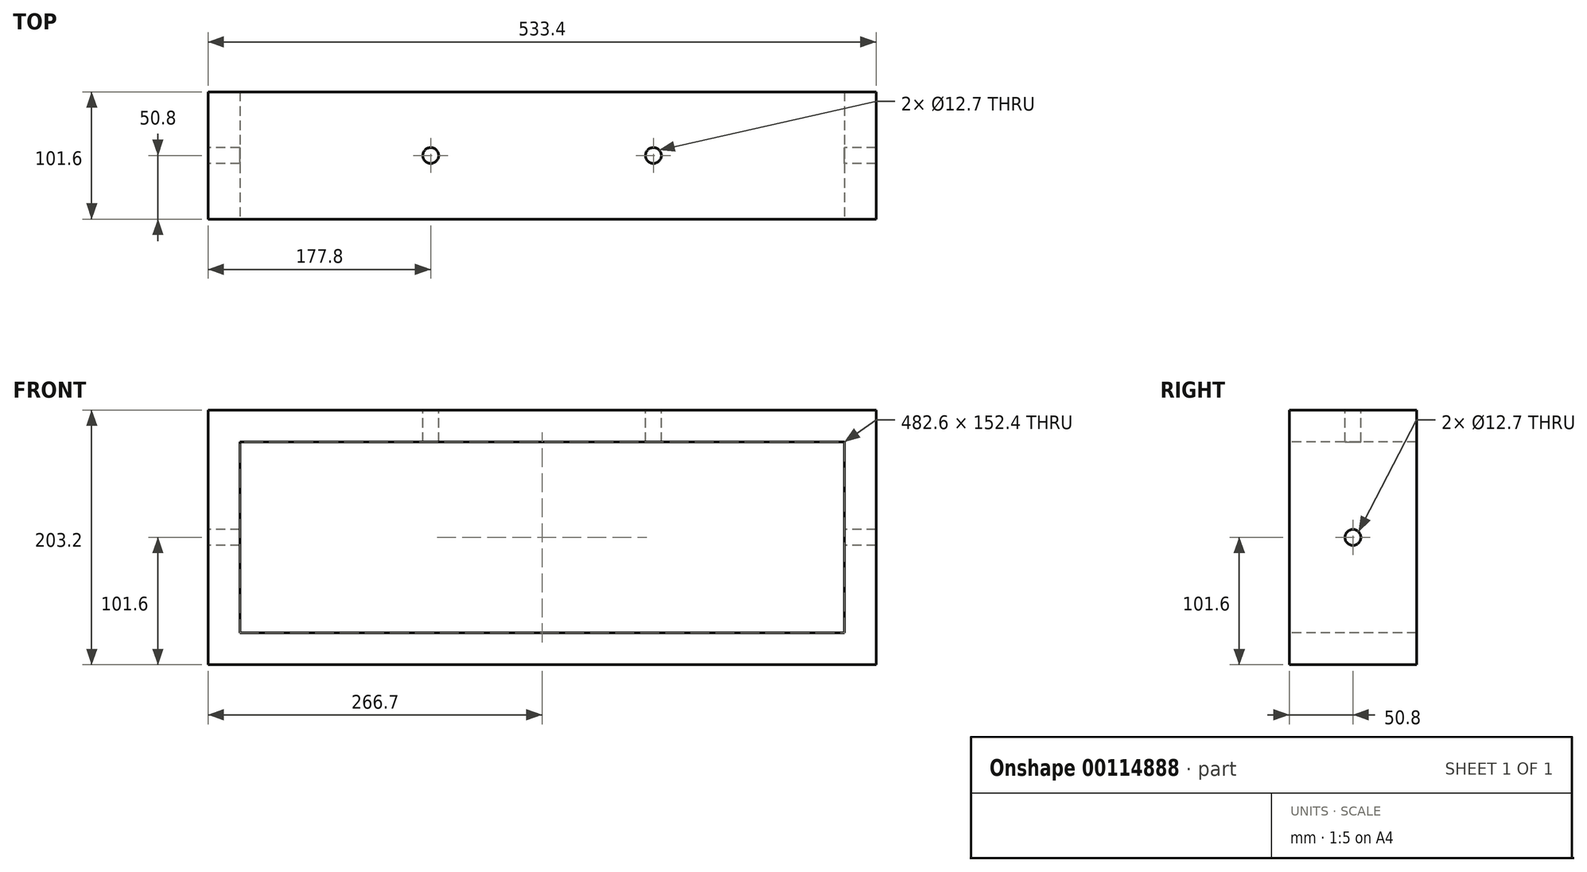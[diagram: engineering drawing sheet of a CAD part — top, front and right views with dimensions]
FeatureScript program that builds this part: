
annotation { "Feature Type Name" : "Feature", "Feature Type Description" : "" }
export const myFeature = defineFeature(function(context is Context, id is Id, definition is map)
    precondition{}
    {
        {
            var Q0;
            Q0=qCreatedBy(makeId("Front.planeOp"),FACE);
            var sketch = newSketch(context, id + "F0", { "sketchPlane" : qUnion([Q0])});
            skLineSegment(sketch, "E0.bottom", {"start": v(-266.7, 101.6) * mm, "end": v(266.7, 101.6) * mm});
            skLineSegment(sketch, "E0.top", {"start": v(-266.7, -101.6) * mm, "end": v(266.7, -101.6) * mm});
            skLineSegment(sketch, "E0.left", {"start": v(-266.7, 101.6) * mm, "end": v(-266.7, -101.6) * mm});
            skLineSegment(sketch, "E0.right", {"start": v(266.7, 101.6) * mm, "end": v(266.7, -101.6) * mm});
            skPoint(sketch, "E0.middle", {"position": v(0, 0) * mm});
            skLineSegment(sketch, "E1", {"start": v(-266.7, 101.6) * mm, "end": v(-266.7, 76.2) * mm});
            skLineSegment(sketch, "E2", {"start": v(-266.7, 76.2) * mm, "end": v(266.7, 76.2) * mm});
            skLineSegment(sketch, "E3", {"start": v(-266.7, 76.2) * mm, "end": v(-241.3, 76.2) * mm});
            skLineSegment(sketch, "E4", {"start": v(-241.3, 76.2) * mm, "end": v(-241.3, -101.6) * mm});
            skLineSegment(sketch, "E5", {"start": v(266.7, 76.2) * mm, "end": v(241.3, 76.2) * mm});
            skLineSegment(sketch, "E6", {"start": v(241.3, 76.2) * mm, "end": v(241.3, -101.6) * mm});
            skLineSegment(sketch, "E7", {"start": v(241.3, -101.6) * mm, "end": v(241.3, -76.2) * mm});
            skLineSegment(sketch, "E8", {"start": v(241.3, -76.2) * mm, "end": v(-241.3, -76.2) * mm});
            skLineSegment(sketch, "E9", {"start": v(-266.7, 76.2) * mm, "end": v(-266.7, -101.6) * mm});
            skSolve(sketch);
        }
        {
            var Q0;
            Q0 = qSketchRegion(id + "F0", true);
            var Q1;
            Q1=makeQuery(id+"F0.imprint","IMPRINT",FACE,{"disambiguationData":[TD([[makeQuery(id+"F0.imprint","IMPRINT",EDGE,{"derivedFrom":sQuery(id+"F0.wireOp",EDGE,"E0.bottom")}),-1.0]])]});
            extrude(context, id + "F1", {"entities" : qUnion([Q0, Q1]), "oppositeDirection" : true, "depth" : 101.6 * mm});
        }
        {
            var Q0;
            Q0=makeQuery(id+"F1.opExtrude","CAP_FACE",FACE,{"disambiguationData":[OSD([sQuery(id+"F0.wireOp",EDGE,"E0.bottom"),sQuery(id+"F0.wireOp",EDGE,"E0.top"),sQuery(id+"F0.wireOp",EDGE,"E0.left"),sQuery(id+"F0.wireOp",EDGE,"E0.right")])],"isStart":true});
            var sketch = newSketch(context, id + "F2", { "sketchPlane" : qUnion([Q0])});
            skLineSegment(sketch, "E10.bottom", {"start": v(241.3, 76.2) * mm, "end": v(-241.3, 76.2) * mm});
            skLineSegment(sketch, "E10.top", {"start": v(241.3, -76.2) * mm, "end": v(-241.3, -76.2) * mm});
            skLineSegment(sketch, "E10.left", {"start": v(241.3, 76.2) * mm, "end": v(241.3, -76.2) * mm});
            skLineSegment(sketch, "E10.right", {"start": v(-241.3, 76.2) * mm, "end": v(-241.3, -76.2) * mm});
            skPoint(sketch, "E10.middle", {"position": v(0, 0) * mm});
            skSolve(sketch);
        }
        {
            var Q0;
            Q0 = qSketchRegion(id + "F2", true);
            extrude(context, id + "F3", {"entities" : qUnion([Q0]), "operationType" : NewBodyOperationType.REMOVE, "oppositeDirection" : true, "depth" : 101.6 * mm});
        }
        {
            var Q0;
            Q0=qCreatedBy(makeId("Right.planeOp"),FACE);
            var sketch = newSketch(context, id + "F4", { "sketchPlane" : qUnion([Q0])});
            skLineSegment(sketch, "E11", {"start": v(50.8, 101.6) * mm, "end": v(50.8, -101.6) * mm, "construction": true});
            skLineSegment(sketch, "E12", {"start": v(0, 0) * mm, "end": v(101.6, 0) * mm, "construction": true});
            skPoint(sketch, "E13", {"position": v(50.8, 0) * mm});
            skCircle(sketch, "E14", {"center": v(50.8, 0) * mm, "radius": 6.35 * mm});
            skSolve(sketch);
        }
        {
            var Q0;
            Q0=makeQuery(id+"F4.imprint","IMPRINT",FACE,{"disambiguationData":[TD([[makeQuery(id+"F4.imprint","IMPRINT",EDGE,{"derivedFrom":sQuery(id+"F4.wireOp",EDGE,"E14")}),1.0]])]});
            var Q1;
            Q1=sQuery(id+"F4.wireOp",EDGE,"E14");
            extrude(context, id + "F5", {"entities" : qUnion([Q0]), "operationType" : NewBodyOperationType.REMOVE, "surfaceEntities" : qUnion([Q1]), "endBound" : BoundingType.THROUGH_ALL, "depth" : 25.4 * mm, "hasSecondDirection" : true, "secondDirectionBound" : SecondDirectionBoundingType.THROUGH_ALL, "secondDirectionOppositeDirection" : true, "secondDirectionDepth" : 25.4 * mm});
        }
        {
            var Q0;
            Q0=makeQuery(id+"F1.opExtrude","SWEPT_FACE",FACE,{"disambiguationData":[OSD([sQuery(id+"F0.wireOp",EDGE,"E0.bottom")])]});
            var sketch = newSketch(context, id + "F6", { "sketchPlane" : qUnion([Q0])});
            skLineSegment(sketch, "E15", {"start": v(-266.7, 50.8) * mm, "end": v(266.7, 50.8) * mm, "construction": true});
            skLineSegment(sketch, "E16", {"start": v(-266.7, 50.8) * mm, "end": v(-88.9, 50.8) * mm, "construction": true});
            skLineSegment(sketch, "E17", {"start": v(-88.9, 50.8) * mm, "end": v(88.9, 50.8) * mm, "construction": true});
            skLineSegment(sketch, "E18", {"start": v(88.9, 50.8) * mm, "end": v(266.7, 50.8) * mm, "construction": true});
            skLineSegment(sketch, "E19", {"start": v(-88.9, 101.6) * mm, "end": v(-88.9, 0) * mm, "construction": true});
            skLineSegment(sketch, "E20", {"start": v(88.9, 0) * mm, "end": v(88.9, 101.6) * mm, "construction": true});
            skCircle(sketch, "E21", {"center": v(-88.9, 50.8) * mm, "radius": 6.35 * mm});
            skCircle(sketch, "E22", {"center": v(88.9, 50.8) * mm, "radius": 6.35 * mm});
            skSolve(sketch);
        }
        {
            var Q0;
            Q0 = qSketchRegion(id + "F6", true);
            extrude(context, id + "F7", {"entities" : qUnion([Q0]), "operationType" : NewBodyOperationType.REMOVE, "oppositeDirection" : true, "depth" : 25.4 * mm});
        }
    });
